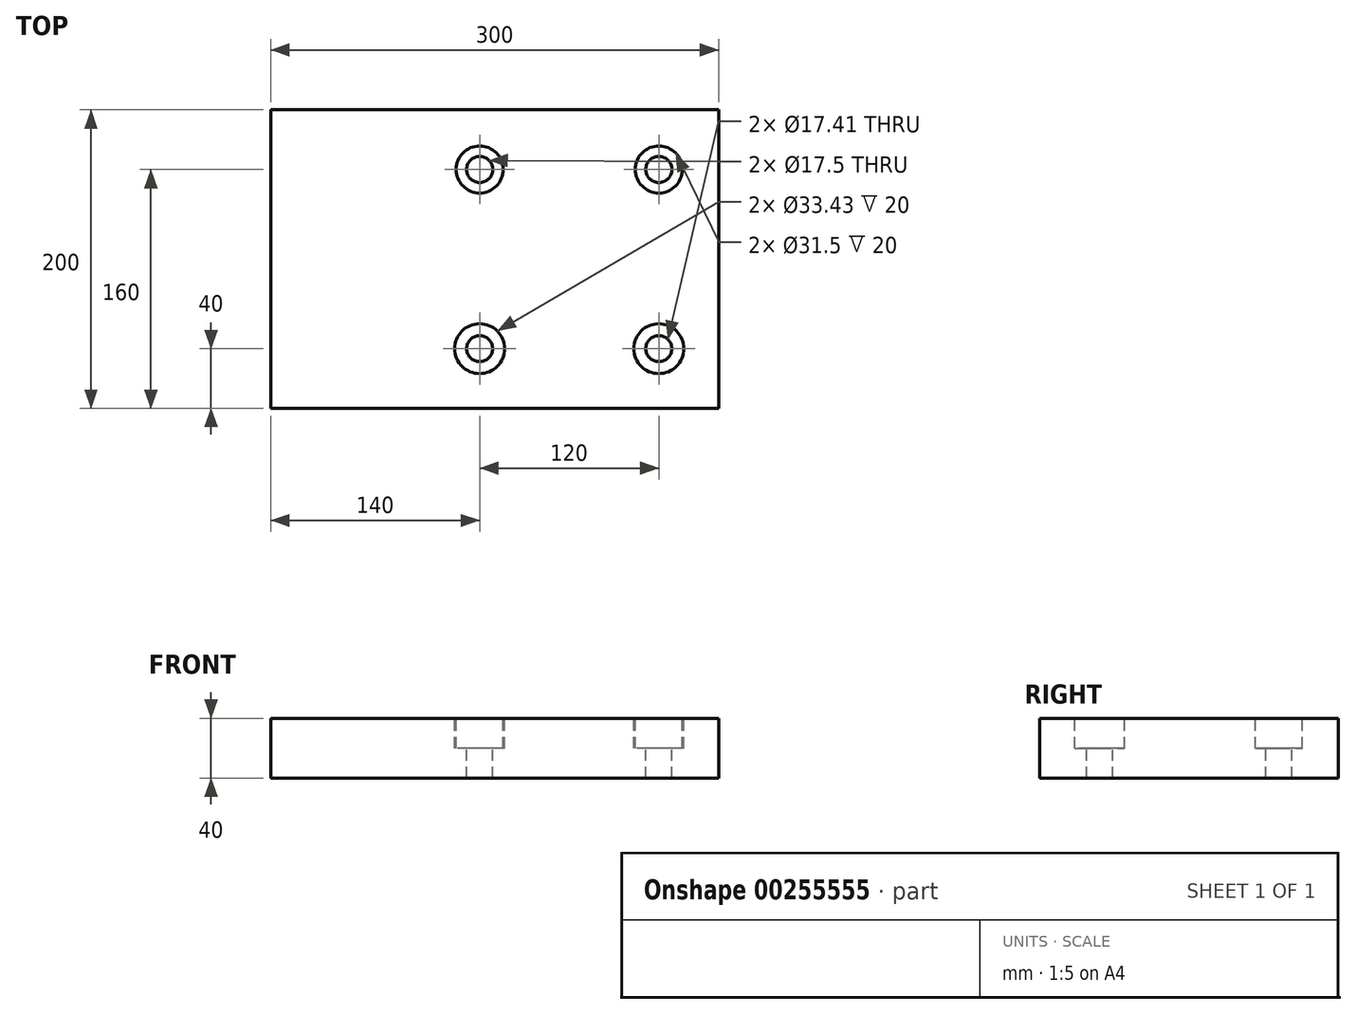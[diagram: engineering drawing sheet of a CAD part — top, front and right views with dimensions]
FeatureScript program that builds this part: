
annotation { "Feature Type Name" : "Feature", "Feature Type Description" : "" }
export const myFeature = defineFeature(function(context is Context, id is Id, definition is map)
    precondition{}
    {
        {
            var Q0;
            Q0=qCreatedBy(makeId("Top.planeOp"),FACE);
            var sketch = newSketch(context, id + "F0", { "sketchPlane" : qUnion([Q0])});
            skLineSegment(sketch, "E0.bottom", {"start": v(-150, 0) * mm, "end": v(150, 0) * mm});
            skLineSegment(sketch, "E0.top", {"start": v(-150, -200) * mm, "end": v(150, -200) * mm});
            skLineSegment(sketch, "E0.left", {"start": v(-150, 0) * mm, "end": v(-150, -200) * mm});
            skLineSegment(sketch, "E0.right", {"start": v(150, 0) * mm, "end": v(150, -200) * mm});
            skCircle(sketch, "E1", {"center": v(-10, -40) * mm, "radius": 15.75 * mm});
            skCircle(sketch, "E2", {"center": v(-10, -160) * mm, "radius": 16.71 * mm});
            skCircle(sketch, "E3", {"center": v(110, -160) * mm, "radius": 16.71 * mm});
            skCircle(sketch, "E4", {"center": v(110, -40) * mm, "radius": 15.75 * mm});
            skCircle(sketch, "E5", {"center": v(-10, -40) * mm, "radius": 8.75 * mm});
            skCircle(sketch, "E6", {"center": v(-10, -160) * mm, "radius": 8.7 * mm});
            skCircle(sketch, "E7", {"center": v(110, -160) * mm, "radius": 8.7 * mm});
            skCircle(sketch, "E8", {"center": v(110, -40) * mm, "radius": 8.75 * mm});
            skSolve(sketch);
        }
        {
            var Q0;
            Q0=makeQuery(id+"F0.imprint","IMPRINT",FACE,{"disambiguationData":[TD([[makeQuery(id+"F0.imprint","IMPRINT",EDGE,{"derivedFrom":sQuery(id+"F0.wireOp",EDGE,"E4")}),1.0]])]});
            var Q1;
            Q1=makeQuery(id+"F0.imprint","IMPRINT",FACE,{"disambiguationData":[TD([[makeQuery(id+"F0.imprint","IMPRINT",EDGE,{"derivedFrom":sQuery(id+"F0.wireOp",EDGE,"E1")}),1.0]])]});
            var Q2;
            Q2=makeQuery(id+"F0.imprint","IMPRINT",FACE,{"disambiguationData":[TD([[makeQuery(id+"F0.imprint","IMPRINT",EDGE,{"derivedFrom":sQuery(id+"F0.wireOp",EDGE,"E2")}),1.0]])]});
            var Q3;
            Q3=makeQuery(id+"F0.imprint","IMPRINT",FACE,{"disambiguationData":[TD([[makeQuery(id+"F0.imprint","IMPRINT",EDGE,{"derivedFrom":sQuery(id+"F0.wireOp",EDGE,"E3")}),1.0]])]});
            var Q4;
            Q4=makeQuery(id+"F0.imprint","IMPRINT",FACE,{"disambiguationData":[TD([[makeQuery(id+"F0.imprint","IMPRINT",EDGE,{"derivedFrom":sQuery(id+"F0.wireOp",EDGE,"E0.bottom")}),-1.0]])]});
            extrude(context, id + "F1", {"entities" : qUnion([Q0, Q1, Q2, Q3, Q4]), "oppositeDirection" : true, "depth" : 40 * mm});
        }
        {
            var Q0;
            Q0=makeQuery(id+"F0.imprint","IMPRINT",FACE,{"disambiguationData":[TD([[makeQuery(id+"F0.imprint","IMPRINT",EDGE,{"derivedFrom":sQuery(id+"F0.wireOp",EDGE,"E2")}),1.0]])]});
            var Q1;
            Q1=makeQuery(id+"F0.imprint","IMPRINT",FACE,{"disambiguationData":[TD([[makeQuery(id+"F0.imprint","IMPRINT",EDGE,{"derivedFrom":sQuery(id+"F0.wireOp",EDGE,"E3")}),1.0]])]});
            var Q2;
            Q2=makeQuery(id+"F0.imprint","IMPRINT",FACE,{"disambiguationData":[TD([[makeQuery(id+"F0.imprint","IMPRINT",EDGE,{"derivedFrom":sQuery(id+"F0.wireOp",EDGE,"E1")}),1.0]])]});
            var Q3;
            Q3=makeQuery(id+"F0.imprint","IMPRINT",FACE,{"disambiguationData":[TD([[makeQuery(id+"F0.imprint","IMPRINT",EDGE,{"derivedFrom":sQuery(id+"F0.wireOp",EDGE,"E4")}),1.0]])]});
            extrude(context, id + "F2", {"entities" : qUnion([Q0, Q1, Q2, Q3]), "operationType" : NewBodyOperationType.REMOVE, "oppositeDirection" : true, "depth" : 20 * mm});
        }
    });
